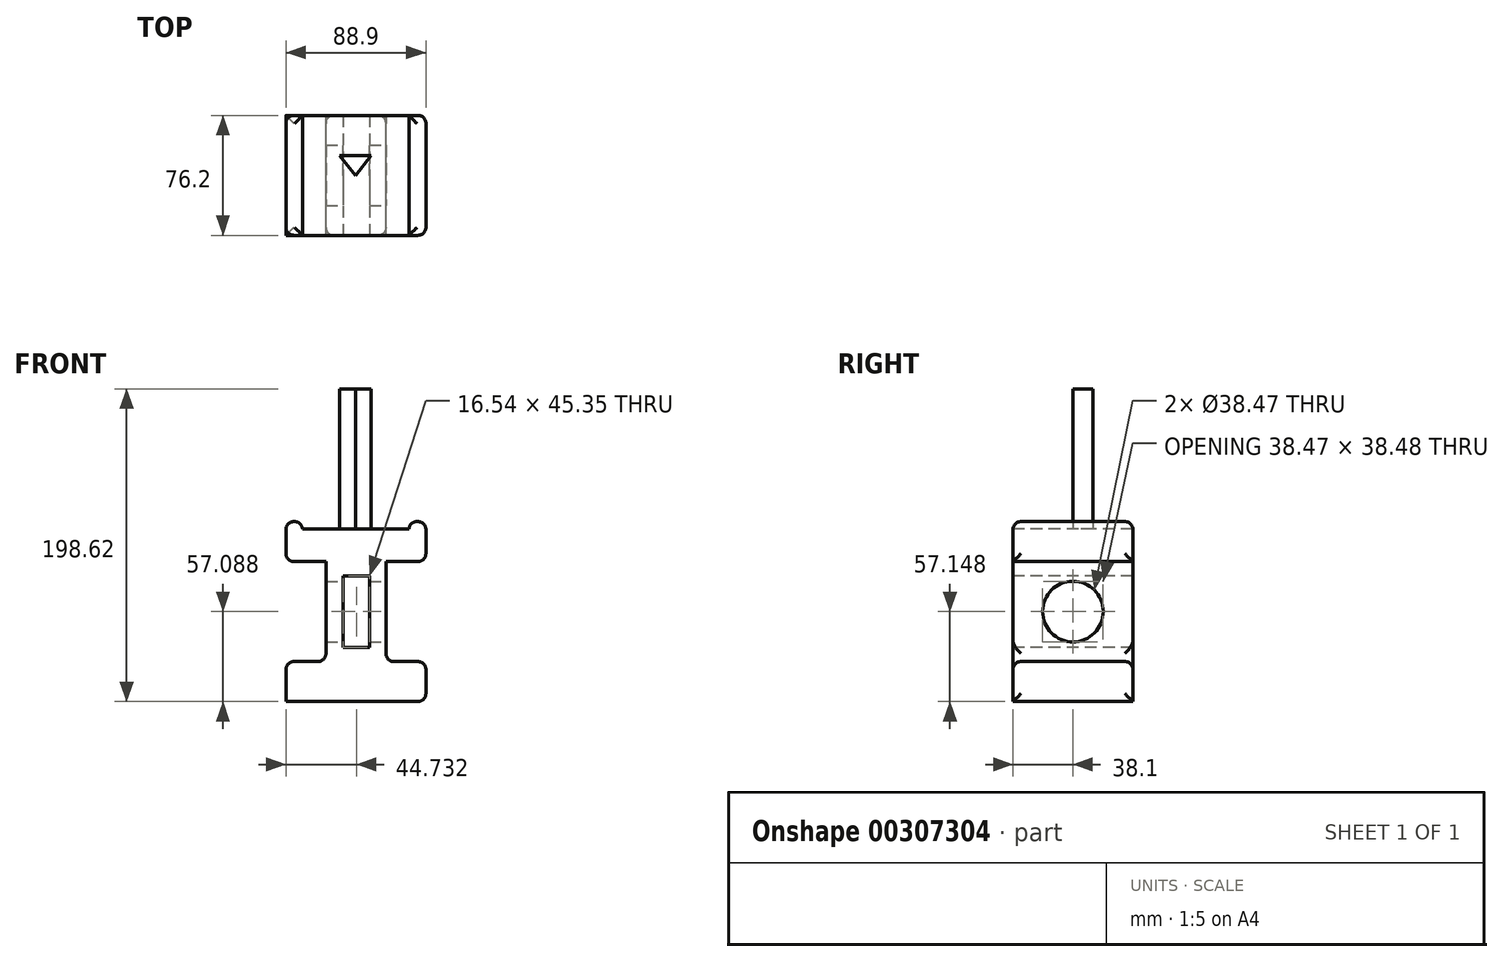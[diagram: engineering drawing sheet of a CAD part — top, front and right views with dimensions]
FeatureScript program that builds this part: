
annotation { "Feature Type Name" : "Feature", "Feature Type Description" : "" }
export const myFeature = defineFeature(function(context is Context, id is Id, definition is map)
    precondition{}
    {
        {
            var Q0;
            Q0=qCreatedBy(makeId("Front.planeOp"),FACE);
            var sketch = newSketch(context, id + "F0", { "sketchPlane" : qUnion([Q0])});
            skLineSegment(sketch, "E0", {"start": v(-22.47, 12.7) * mm, "end": v(-22.47, -50.8) * mm});
            skLineSegment(sketch, "E1", {"start": v(-47.87, -50.8) * mm, "end": v(-47.87, -76.2) * mm});
            skLineSegment(sketch, "E2", {"start": v(-47.87, -76.2) * mm, "end": v(-47.87, -50.8) * mm});
            skLineSegment(sketch, "E3", {"start": v(-22.47, -50.8) * mm, "end": v(-47.87, -50.8) * mm});
            skLineSegment(sketch, "E4", {"start": v(-47.87, -76.2) * mm, "end": v(41.03, -76.2) * mm});
            skLineSegment(sketch, "E5", {"start": v(41.03, -76.2) * mm, "end": v(41.03, -50.8) * mm});
            skLineSegment(sketch, "E6", {"start": v(41.03, -50.8) * mm, "end": v(15.63, -50.8) * mm});
            skLineSegment(sketch, "E7", {"start": v(15.63, -50.8) * mm, "end": v(15.63, 12.7) * mm});
            skLineSegment(sketch, "E8", {"start": v(15.63, 12.7) * mm, "end": v(41.03, 12.7) * mm});
            skLineSegment(sketch, "E9", {"start": v(41.03, 12.7) * mm, "end": v(41.03, 38.1) * mm});
            skLineSegment(sketch, "E10", {"start": v(41.03, 38.1) * mm, "end": v(-47.87, 38.1) * mm});
            skLineSegment(sketch, "E11", {"start": v(-47.87, 38.1) * mm, "end": v(-47.87, 12.7) * mm});
            skLineSegment(sketch, "E12", {"start": v(-47.87, 12.7) * mm, "end": v(-22.47, 12.7) * mm});
            skSolve(sketch);
        }
        {
            var Q0;
            Q0=makeQuery(id+"F0.imprint","IMPRINT",FACE,{"disambiguationData":[TD([[makeQuery(id+"F0.imprint","IMPRINT",EDGE,{"derivedFrom":sQuery(id+"F0.wireOp",EDGE,"E0")}),1.0]])]});
            extrude(context, id + "F1", {"entities" : qUnion([Q0]), "depth" : 76.2 * mm});
        }
        {
            var Q0;
            Q0=makeQuery(id+"F1.opExtrude","SWEPT_FACE",FACE,{"disambiguationData":[OSD([sQuery(id+"F0.wireOp",EDGE,"E7")])]});
            var sketch = newSketch(context, id + "F2", { "sketchPlane" : qUnion([Q0])});
            skCircle(sketch, "E13", {"center": v(-38.1, -19.05) * mm, "radius": 19.24 * mm});
            skPoint(sketch, "E13.centerSnap0", {"position": v(-76.2, -19.05) * mm});
            skPoint(sketch, "E13.centerSnap1", {"position": v(-38.1, 12.7) * mm});
            skSolve(sketch);
        }
        {
            var Q0;
            Q0=makeQuery(id+"F2.imprint","IMPRINT",FACE,{"disambiguationData":[TD([[makeQuery(id+"F2.imprint","IMPRINT",EDGE,{"derivedFrom":sQuery(id+"F2.wireOp",EDGE,"E13")}),1.0]])]});
            var Q1;
            {var subQ0=sQuery(id+"FS2Dw36osFLuSWb_1.wireOp",EDGE,"Aigw20a4-v98Q-E5uy-Eh7q-ToeRDlIaiQWf");var subQ1=makeQuery(id+"F1.opExtrude","CAP_EDGE",EDGE,{"disambiguationData":[OSD([sQuery(id+"F0.wireOp",EDGE,"E0")])],"isStart":false});var subQ2=makeQuery(id+"FS2Dw36osFLuSWb_1.imprint","INTERSECT",VERTEX,{"disambiguationData":[OD(0.0)],"derivedFrom":[subQ1,subQ0]});Q1=makeQuery(id+"FS2Dw36osFLuSWb_1.imprint","IMPRINT",FACE,{"disambiguationData":[TD([[makeQuery(id+"FS2Dw36osFLuSWb_1.imprint","IMPRINT",EDGE,{"disambiguationData":[TD([[subQ2,-1.0]])],"derivedFrom":subQ0}),1.0]])]});}
            extrude(context, id + "F3", {"entities" : qUnion([Q0, Q1]), "operationType" : NewBodyOperationType.REMOVE, "endBound" : BoundingType.THROUGH_ALL, "oppositeDirection" : true, "depth" : 25.4 * mm});
        }
        {
            var Q0;
            Q0=makeQuery(id+"F1.opExtrude","CAP_FACE",FACE,{"disambiguationData":[OSD([sQuery(id+"F0.wireOp",EDGE,"E0"),sQuery(id+"F0.wireOp",EDGE,"E2"),sQuery(id+"F0.wireOp",EDGE,"E3"),sQuery(id+"F0.wireOp",EDGE,"E4"),sQuery(id+"F0.wireOp",EDGE,"E5"),sQuery(id+"F0.wireOp",EDGE,"E6"),sQuery(id+"F0.wireOp",EDGE,"E7"),sQuery(id+"F0.wireOp",EDGE,"E8"),sQuery(id+"F0.wireOp",EDGE,"E9"),sQuery(id+"F0.wireOp",EDGE,"E10"),sQuery(id+"F0.wireOp",EDGE,"E11"),sQuery(id+"F0.wireOp",EDGE,"E12")])],"isStart":false});
            var sketch = newSketch(context, id + "F4", { "sketchPlane" : qUnion([Q0])});
            skLineSegment(sketch, "E14.bottom", {"start": v(-11.4, 3.56) * mm, "end": v(5.13, 3.56) * mm});
            skLineSegment(sketch, "E14.top", {"start": v(-11.4, -41.79) * mm, "end": v(5.13, -41.79) * mm});
            skLineSegment(sketch, "E14.left", {"start": v(-11.4, 3.56) * mm, "end": v(-11.4, -41.79) * mm});
            skLineSegment(sketch, "E14.right", {"start": v(5.13, 3.56) * mm, "end": v(5.13, -41.79) * mm});
            skSolve(sketch);
        }
        {
            var Q0;
            Q0=makeQuery(id+"F4.imprint","IMPRINT",FACE,{"disambiguationData":[TD([[makeQuery(id+"F4.imprint","IMPRINT",EDGE,{"derivedFrom":sQuery(id+"F4.wireOp",EDGE,"E14.bottom")}),-1.0]])]});
            extrude(context, id + "F5", {"entities" : qUnion([Q0]), "operationType" : NewBodyOperationType.REMOVE, "endBound" : BoundingType.THROUGH_ALL, "oppositeDirection" : true, "depth" : 25.4 * mm});
        }
        {
            var Q0;
            Q0=makeQuery(id+"F1.opExtrude","CAP_FACE",FACE,{"disambiguationData":[OSD([sQuery(id+"F0.wireOp",EDGE,"E0"),sQuery(id+"F0.wireOp",EDGE,"E2"),sQuery(id+"F0.wireOp",EDGE,"E3"),sQuery(id+"F0.wireOp",EDGE,"E4"),sQuery(id+"F0.wireOp",EDGE,"E5"),sQuery(id+"F0.wireOp",EDGE,"E6"),sQuery(id+"F0.wireOp",EDGE,"E7"),sQuery(id+"F0.wireOp",EDGE,"E8"),sQuery(id+"F0.wireOp",EDGE,"E9"),sQuery(id+"F0.wireOp",EDGE,"E10"),sQuery(id+"F0.wireOp",EDGE,"E11"),sQuery(id+"F0.wireOp",EDGE,"E12")])],"isStart":false});
            var sketch = newSketch(context, id + "F6", { "sketchPlane" : qUnion([Q0])});
            skLineSegment(sketch, "E15.bottom", {"start": v(-37.37, 40.93) * mm, "end": v(30.24, 40.93) * mm});
            skLineSegment(sketch, "E15.top", {"start": v(-37.37, 33.52) * mm, "end": v(30.24, 33.52) * mm});
            skLineSegment(sketch, "E15.left", {"start": v(-37.37, 40.93) * mm, "end": v(-37.37, 33.52) * mm});
            skLineSegment(sketch, "E15.right", {"start": v(30.24, 40.93) * mm, "end": v(30.24, 33.52) * mm});
            skSolve(sketch);
        }
        {
            var Q0;
            {var subQ0=sQuery(id+"F6.wireOp",EDGE,"E15.top");Q0=makeQuery(id+"F6.imprint","IMPRINT",FACE,{"disambiguationData":[TD([[makeQuery(id+"F6.imprint","IMPRINT",EDGE,{"derivedFrom":subQ0}),1.0]])]});}
            extrude(context, id + "F7", {"entities" : qUnion([Q0]), "operationType" : NewBodyOperationType.REMOVE, "endBound" : BoundingType.THROUGH_ALL, "oppositeDirection" : true, "depth" : 25.4 * mm});
        }
        {
            var Q0;
            {var subQ2=sQuery(id+"F0.wireOp",EDGE,"E10");var subQ3=sQuery(id+"F0.wireOp",EDGE,"E9");Q0=makeQuery(id+"F7.boolean.opBoolean","SPLIT",FACE,{"disambiguationData":[TD([makeQuery(id+"F1.opExtrude","SWEPT_FACE",FACE,{"disambiguationData":[OSD([subQ3])]})])],"derivedFrom":makeQuery(id+"F1.opExtrude","SWEPT_FACE",FACE,{"disambiguationData":[OSD([subQ2])]})});}
            var Q1;
            Q1=makeQuery(id+"F1.opExtrude","SWEPT_FACE",FACE,{"disambiguationData":[OSD([sQuery(id+"F0.wireOp",EDGE,"E9")])]});
            fillet(context, id + "F8", {"entities" : qUnion([Q0, Q1]), "radius" : 5.08 * mm, "tangentPropagation" : true, "allowEdgeOverflow" : false});
        }
        {
            var Q0;
            {var subQ1=sQuery(id+"F0.wireOp",EDGE,"E11");var subQ2=sQuery(id+"F0.wireOp",EDGE,"E10");Q0=makeQuery(id+"F7.boolean.opBoolean","SPLIT",FACE,{"disambiguationData":[TD([makeQuery(id+"F1.opExtrude","SWEPT_FACE",FACE,{"disambiguationData":[OSD([subQ1])]})])],"derivedFrom":makeQuery(id+"F1.opExtrude","SWEPT_FACE",FACE,{"disambiguationData":[OSD([subQ2])]})});}
            var Q1;
            Q1=makeQuery(id+"F1.opExtrude","SWEPT_FACE",FACE,{"disambiguationData":[OSD([sQuery(id+"F0.wireOp",EDGE,"E11")])]});
            fillet(context, id + "F9", {"entities" : qUnion([Q0, Q1]), "radius" : 5.08 * mm, "tangentPropagation" : true, "allowEdgeOverflow" : false});
        }
        {
            var Q0;
            Q0=makeQuery(id+"F1.opExtrude","SWEPT_FACE",FACE,{"disambiguationData":[OSD([sQuery(id+"F0.wireOp",EDGE,"E3")])]});
            var Q1;
            Q1=makeQuery(id+"F1.opExtrude","SWEPT_FACE",FACE,{"disambiguationData":[OSD([sQuery(id+"F0.wireOp",EDGE,"E2")])]});
            var Q2;
            Q2=makeQuery(id+"F1.opExtrude","SWEPT_FACE",FACE,{"disambiguationData":[OSD([sQuery(id+"F0.wireOp",EDGE,"E6")])]});
            var Q3;
            Q3=makeQuery(id+"F1.opExtrude","SWEPT_FACE",FACE,{"disambiguationData":[OSD([sQuery(id+"F0.wireOp",EDGE,"E5")])]});
            fillet(context, id + "F10", {"entities" : qUnion([Q0, Q1, Q2, Q3]), "radius" : 5.08 * mm, "tangentPropagation" : true, "allowEdgeOverflow" : false});
        }
        {
            var Q0;
            Q0=makeQuery(id+"F7.boolean.opBoolean","COPY",FACE,{"derivedFrom":makeQuery(id+"F7.opExtrude","SWEPT_FACE",FACE,{"disambiguationData":[OSD([sQuery(id+"F6.wireOp",EDGE,"E15.top")])]})});
            var sketch = newSketch(context, id + "F11", { "sketchPlane" : qUnion([Q0])});
            skLineSegment(sketch, "E16", {"start": v(-3.57, -38.1) * mm, "end": v(-13.7, -25.53) * mm});
            skPoint(sketch, "E16.startSnap0", {"position": v(-37.37, -38.1) * mm});
            skPoint(sketch, "E16.startSnap1", {"position": v(-3.57, -0.02) * mm});
            skLineSegment(sketch, "E17", {"start": v(-13.7, -25.53) * mm, "end": v(6.28, -25.53) * mm});
            skLineSegment(sketch, "E18", {"start": v(6.28, -25.53) * mm, "end": v(-3.57, -38.1) * mm});
            skSolve(sketch);
        }
        {
            var Q0;
            Q0=makeQuery(id+"F11.imprint","IMPRINT",FACE,{"disambiguationData":[TD([[makeQuery(id+"F11.imprint","IMPRINT",EDGE,{"derivedFrom":sQuery(id+"F11.wireOp",EDGE,"E16")}),-1.0]])]});
            extrude(context, id + "F12", {"entities" : qUnion([Q0]), "operationType" : NewBodyOperationType.ADD, "depth" : 88.9 * mm});
        }
    });
